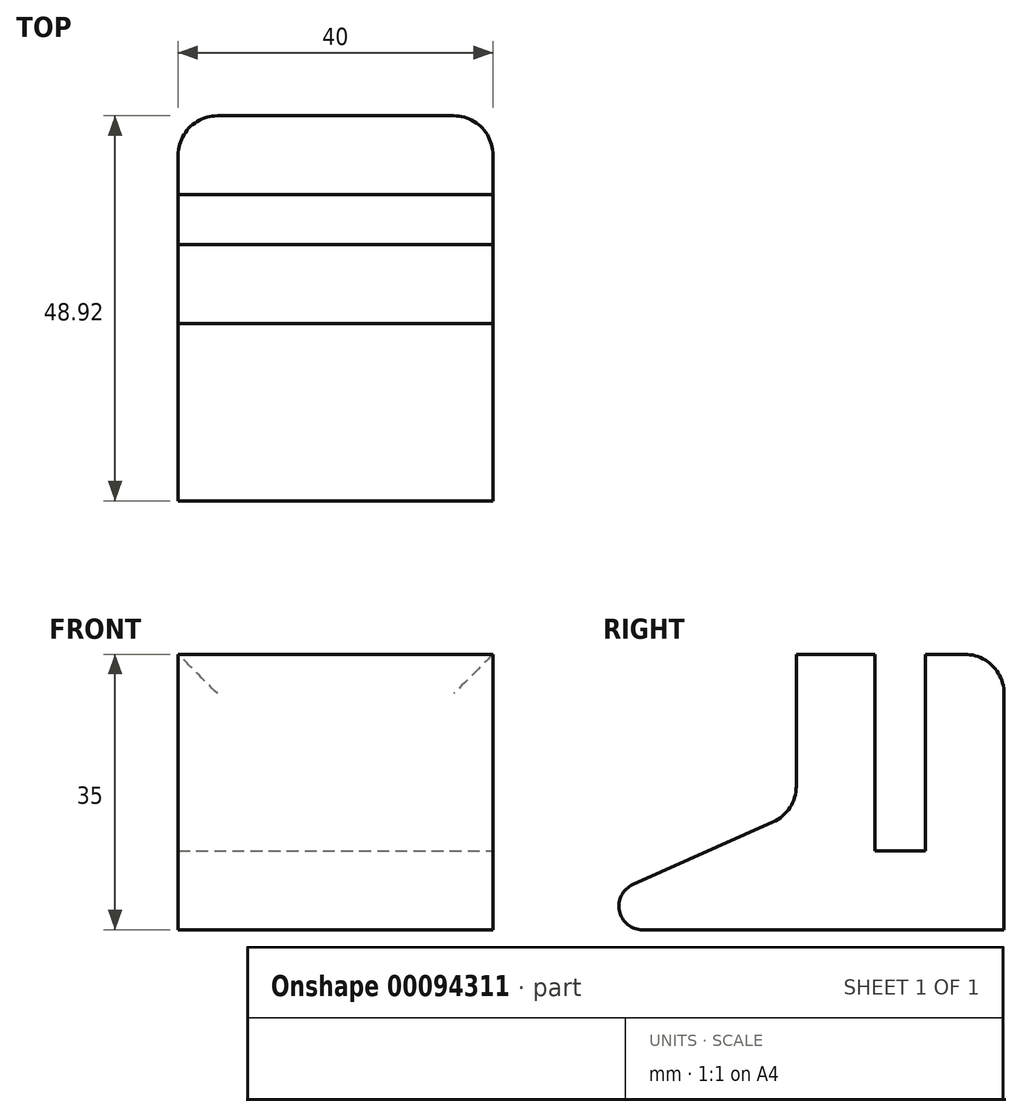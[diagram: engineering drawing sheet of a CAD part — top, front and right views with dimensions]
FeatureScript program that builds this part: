
annotation { "Feature Type Name" : "Feature", "Feature Type Description" : "" }
export const myFeature = defineFeature(function(context is Context, id is Id, definition is map)
    precondition{}
    {
        {
            var Q0;
            Q0=qCreatedBy(makeId("Top.planeOp"),FACE);
            var sketch = newSketch(context, id + "F0", { "sketchPlane" : qUnion([Q0])});
            skLineSegment(sketch, "E0.bottom", {"start": v(20, 30) * mm, "end": v(-20, 30) * mm});
            skLineSegment(sketch, "E0.top", {"start": v(20, -30) * mm, "end": v(-20, -30) * mm});
            skLineSegment(sketch, "E0.left", {"start": v(20, 30) * mm, "end": v(20, -30) * mm});
            skLineSegment(sketch, "E0.right", {"start": v(-20, 30) * mm, "end": v(-20, -30) * mm});
            skPoint(sketch, "E0.middle", {"position": v(0, 0) * mm});
            skSolve(sketch);
        }
        {
            var Q0;
            Q0 = qSketchRegion(id + "F0", true);
            extrude(context, id + "F1", {"entities" : qUnion([Q0]), "depth" : 10 * mm});
        }
        {
            var Q0;
            Q0=makeQuery(id+"F1.opExtrude","CAP_FACE",FACE,{"disambiguationData":[OSD([sQuery(id+"F0.wireOp",EDGE,"E0.bottom"),sQuery(id+"F0.wireOp",EDGE,"E0.top"),sQuery(id+"F0.wireOp",EDGE,"E0.left"),sQuery(id+"F0.wireOp",EDGE,"E0.right")])],"isStart":false});
            var sketch = newSketch(context, id + "F2", { "sketchPlane" : qUnion([Q0])});
            skLineSegment(sketch, "E1.bottom", {"start": v(-20, 30) * mm, "end": v(20, 30) * mm});
            skLineSegment(sketch, "E1.top", {"start": v(-20, 20) * mm, "end": v(20, 20) * mm});
            skLineSegment(sketch, "E1.left", {"start": v(-20, 30) * mm, "end": v(-20, 20) * mm});
            skLineSegment(sketch, "E1.right", {"start": v(20, 30) * mm, "end": v(20, 20) * mm});
            skLineSegment(sketch, "E2.bottom", {"start": v(-20, -30) * mm, "end": v(20, -30) * mm});
            skLineSegment(sketch, "E2.top", {"start": v(-20, 13.6) * mm, "end": v(20, 13.6) * mm});
            skLineSegment(sketch, "E2.left", {"start": v(-20, -30) * mm, "end": v(-20, 13.6) * mm});
            skLineSegment(sketch, "E2.right", {"start": v(20, -30) * mm, "end": v(20, 13.6) * mm});
            skSolve(sketch);
        }
        {
            var Q0;
            Q0=makeQuery(id+"F2.imprint","IMPRINT",FACE,{"disambiguationData":[TD([[makeQuery(id+"F2.imprint","IMPRINT",EDGE,{"derivedFrom":sQuery(id+"F2.wireOp",EDGE,"E1.bottom")}),1.0]])]});
            var Q1;
            Q1=makeQuery(id+"F2.imprint","IMPRINT",FACE,{"disambiguationData":[TD([[makeQuery(id+"F2.imprint","IMPRINT",EDGE,{"derivedFrom":sQuery(id+"F2.wireOp",EDGE,"E2.bottom")}),-1.0]])]});
            extrude(context, id + "F3", {"entities" : qUnion([Q0, Q1]), "operationType" : NewBodyOperationType.ADD, "depth" : 25 * mm});
        }
        {
            var Q0;
            Q0=makeQuery(id+"F3.boolean.opBoolean","MERGE",FACE,{"derivedFrom":[makeQuery(id+"F1.opExtrude","SWEPT_FACE",FACE,{"disambiguationData":[OSD([sQuery(id+"F0.wireOp",EDGE,"E0.right")])]}),makeQuery(id+"F3.opExtrude","SWEPT_FACE",FACE,{"disambiguationData":[OSD([sQuery(id+"F2.wireOp",EDGE,"E1.left")])]}),makeQuery(id+"F3.opExtrude","SWEPT_FACE",FACE,{"disambiguationData":[OSD([sQuery(id+"F2.wireOp",EDGE,"E2.left")])]})]});
            var sketch = newSketch(context, id + "F4", { "sketchPlane" : qUnion([Q0])});
            skLineSegment(sketch, "E3", {"start": v(-13.6, 35) * mm, "end": v(-3.6, 35) * mm});
            skLineSegment(sketch, "E4", {"start": v(-3.6, 35) * mm, "end": v(-3.6, 18.24) * mm});
            skLineSegment(sketch, "E5", {"start": v(-0.64, 13.68) * mm, "end": v(30, 0) * mm});
            skPoint(sketch, "E6.visualSharp", {"position": v(-3.6, 15) * mm});
            skArc(sketch, "E6.filletArc", {"start": v(-3.6, 18.24) * mm, "mid": v(-2.8, 15.52) * mm, "end": v(-0.64, 13.68) * mm});
            skSolve(sketch);
        }
        {
            var Q0;
            {var subQ0=sQuery(id+"F4.wireOp",EDGE,"E4");Q0=makeQuery(id+"F4.imprint","IMPRINT",FACE,{"disambiguationData":[TD([[makeQuery(id+"F4.imprint","IMPRINT",EDGE,{"derivedFrom":subQ0}),1.0]])]});}
            extrude(context, id + "F5", {"entities" : qUnion([Q0]), "operationType" : NewBodyOperationType.REMOVE, "oppositeDirection" : true, "depth" : 40 * mm});
        }
        {
            var Q0;
            Q0=makeQuery(id+"F5.boolean.opBoolean","COPY",EDGE,{"derivedFrom":makeQuery(id+"F5.opExtrude","SWEPT_EDGE",EDGE,{"disambiguationData":[OSD([sQuery(id+"F2.wireOp",EDGE,"E2.left"),sQuery(id+"F4.wireOp",EDGE,"E3"),sQuery(id+"F4.wireOp",EDGE,"E4")])]})});
            var Q1;
            Q1=makeQuery(id+"F5.boolean.opBoolean","COPY",EDGE,{"derivedFrom":makeQuery(id+"F5.opExtrude","SWEPT_EDGE",EDGE,{"disambiguationData":[OSD([sQuery(id+"F4.wireOp",EDGE,"E4"),sQuery(id+"F4.wireOp",EDGE,"E5")])]})});
            var Q2;
            Q2=makeQuery(id+"F5.boolean.opBoolean","COPY",EDGE,{"derivedFrom":makeQuery(id+"F5.opExtrude","CAP_EDGE",EDGE,{"disambiguationData":[OSD([sQuery(id+"F4.wireOp",EDGE,"E5")])],"isStart":true})});
            var Q3;
            Q3=makeQuery(id+"F5.boolean.opBoolean","COPY",EDGE,{"derivedFrom":makeQuery(id+"F5.opExtrude","CAP_EDGE",EDGE,{"disambiguationData":[OSD([sQuery(id+"F4.wireOp",EDGE,"E5")])],"isStart":false})});
            var Q4;
            Q4=makeQuery(id+"F3.boolean.opBoolean","MERGE",EDGE,{"derivedFrom":[makeQuery(id+"F1.opExtrude","SWEPT_EDGE",EDGE,{"disambiguationData":[OSD([sQuery(id+"F0.wireOp",EDGE,"E0.bottom"),sQuery(id+"F0.wireOp",EDGE,"E0.left")])]}),makeQuery(id+"F3.opExtrude","SWEPT_EDGE",EDGE,{"disambiguationData":[OSD([sQuery(id+"F2.wireOp",EDGE,"E1.bottom"),sQuery(id+"F2.wireOp",EDGE,"E1.right")])]})]});
            var Q5;
            Q5=makeQuery(id+"F3.opExtrude","CAP_EDGE",EDGE,{"disambiguationData":[OSD([sQuery(id+"F2.wireOp",EDGE,"E1.bottom")])],"isStart":false});
            var Q6;
            Q6=makeQuery(id+"F3.boolean.opBoolean","MERGE",EDGE,{"derivedFrom":[makeQuery(id+"F1.opExtrude","SWEPT_EDGE",EDGE,{"disambiguationData":[OSD([sQuery(id+"F0.wireOp",EDGE,"E0.bottom"),sQuery(id+"F0.wireOp",EDGE,"E0.right")])]}),makeQuery(id+"F3.opExtrude","SWEPT_EDGE",EDGE,{"disambiguationData":[OSD([sQuery(id+"F2.wireOp",EDGE,"E1.bottom"),sQuery(id+"F2.wireOp",EDGE,"E1.left")])]})]});
            fillet(context, id + "F6", {"entities" : qUnion([Q0, Q1, Q2, Q3, Q4, Q5, Q6]), "radius" : 5 * mm, "tangentPropagation" : true, "allowEdgeOverflow" : false});
        }
        {
            var Q0;
            {var subQ0=sQuery(id+"F0.wireOp",EDGE,"E0.top");Q0=makeQuery(id+"F5.boolean.opBoolean","MERGE",EDGE,{"derivedFrom":[makeQuery(id+"F1.opExtrude","CAP_EDGE",EDGE,{"disambiguationData":[OSD([subQ0])],"isStart":true}),makeQuery(id+"F5.opExtrude","SWEPT_EDGE",EDGE,{"disambiguationData":[OSD([subQ0,sQuery(id+"F0.wireOp",EDGE,"E0.right"),sQuery(id+"F2.wireOp",EDGE,"E2.bottom"),sQuery(id+"F2.wireOp",EDGE,"E2.left"),sQuery(id+"F4.wireOp",EDGE,"E5")])]})]});}
            fillet(context, id + "F7", {"entities" : qUnion([Q0]), "radius" : 3 * mm, "tangentPropagation" : true, "allowEdgeOverflow" : false});
        }
    });
